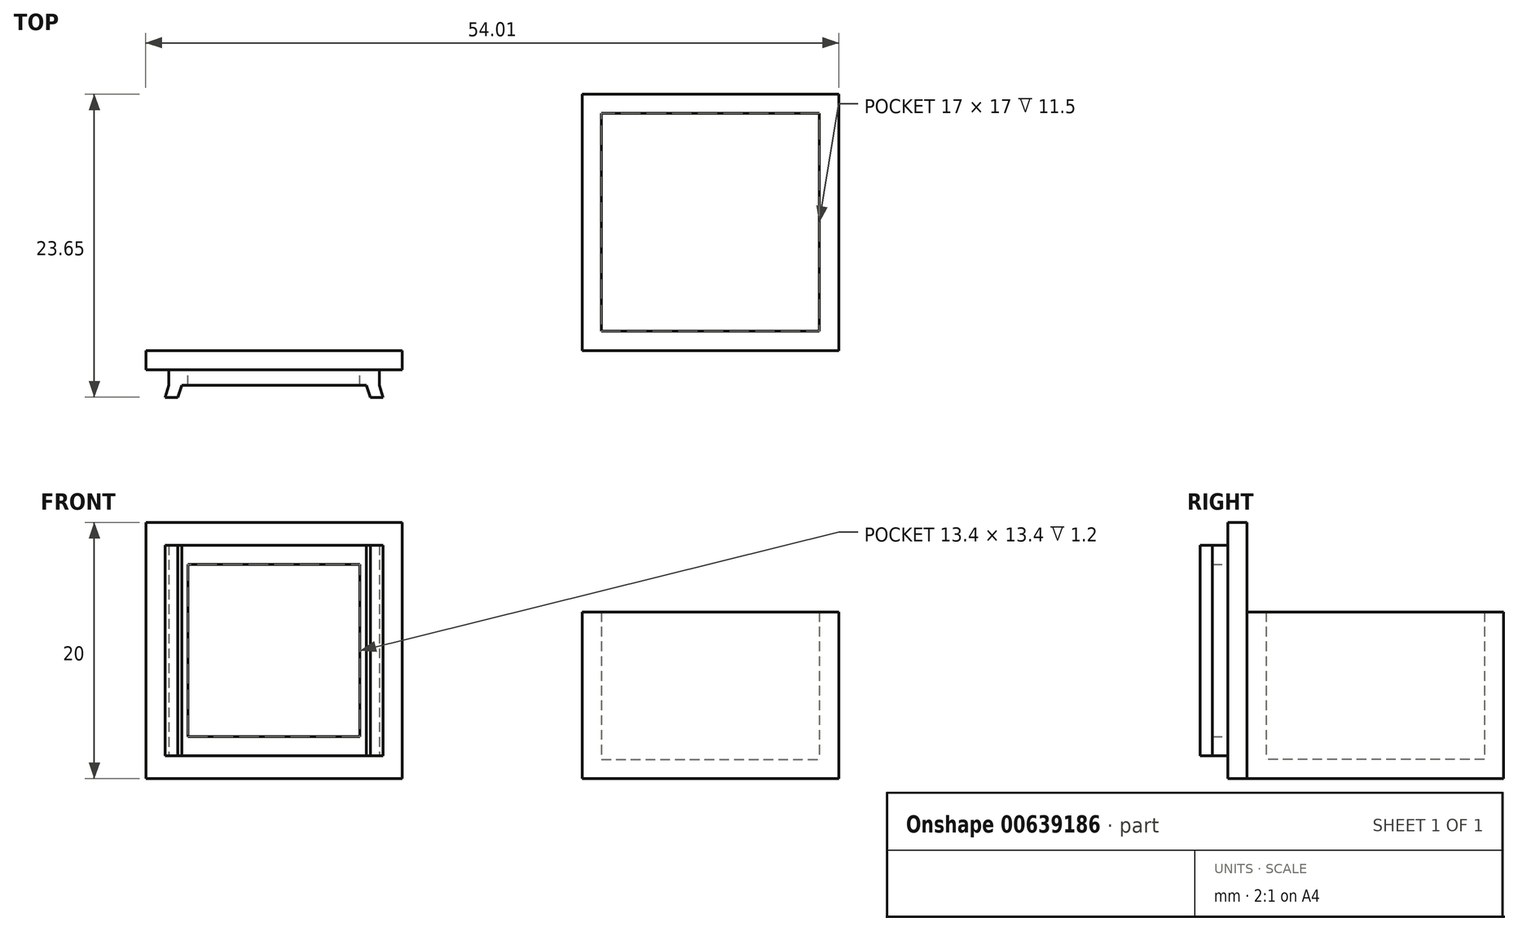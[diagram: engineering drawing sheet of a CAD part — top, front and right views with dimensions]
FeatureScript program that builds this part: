
annotation { "Feature Type Name" : "Feature", "Feature Type Description" : "" }
export const myFeature = defineFeature(function(context is Context, id is Id, definition is map)
    precondition{}
    {
        {
            var Q0;
            Q0=qCreatedBy(makeId("Top.planeOp"),FACE);
            var sketch = newSketch(context, id + "F0", { "sketchPlane" : qUnion([Q0])});
            skLineSegment(sketch, "E0.bottom", {"start": v(0, 0) * mm, "end": v(-20, 0) * mm});
            skLineSegment(sketch, "E0.top", {"start": v(0, 20) * mm, "end": v(-20, 20) * mm});
            skLineSegment(sketch, "E0.left", {"start": v(0, 0) * mm, "end": v(0, 20) * mm});
            skLineSegment(sketch, "E0.right", {"start": v(-20, 0) * mm, "end": v(-20, 20) * mm});
            skSolve(sketch);
        }
        {
            var Q0;
            Q0=makeQuery(id+"F0.imprint","IMPRINT",FACE,{"disambiguationData":[TD([[makeQuery(id+"F0.imprint","IMPRINT",EDGE,{"derivedFrom":sQuery(id+"F0.wireOp",EDGE,"E0.bottom")}),-1.0]])]});
            extrude(context, id + "F1", {"entities" : qUnion([Q0]), "depth" : 1.5 * mm, "offsetDistance" : 25 * mm});
        }
        {
            var Q0;
            Q0=makeQuery(id+"F1.opExtrude","CAP_FACE",FACE,{"disambiguationData":[OSD([sQuery(id+"F0.wireOp",EDGE,"E0.bottom"),sQuery(id+"F0.wireOp",EDGE,"E0.top"),sQuery(id+"F0.wireOp",EDGE,"E0.left"),sQuery(id+"F0.wireOp",EDGE,"E0.right")])],"isStart":false});
            var sketch = newSketch(context, id + "F2", { "sketchPlane" : qUnion([Q0])});
            skLineSegment(sketch, "E1.bottom", {"start": v(-18.5, 18.5) * mm, "end": v(-1.5, 18.5) * mm});
            skLineSegment(sketch, "E1.top", {"start": v(-18.5, 1.5) * mm, "end": v(-1.5, 1.5) * mm});
            skLineSegment(sketch, "E1.left", {"start": v(-18.5, 18.5) * mm, "end": v(-18.5, 1.5) * mm});
            skLineSegment(sketch, "E1.right", {"start": v(-1.5, 18.5) * mm, "end": v(-1.5, 1.5) * mm});
            skSolve(sketch);
        }
        {
            var Q0;
            Q0=makeQuery(id+"F2.imprint","IMPRINT",FACE,{"disambiguationData":[TD([[makeQuery(id+"F2.imprint","IMPRINT",EDGE,{"derivedFrom":sQuery(id+"F2.wireOp",EDGE,"E1.bottom")}),1.0]])]});
            extrude(context, id + "F3", {"entities" : qUnion([Q0]), "operationType" : NewBodyOperationType.ADD, "depth" : 11.5 * mm, "offsetDistance" : 25 * mm});
        }
        {
            var Q0;
            Q0=qCreatedBy(makeId("Front.planeOp"),FACE);
            var sketch = newSketch(context, id + "F4", { "sketchPlane" : qUnion([Q0])});
            skLineSegment(sketch, "E2.bottom", {"start": v(-54, 20) * mm, "end": v(-34, 20) * mm});
            skLineSegment(sketch, "E2.top", {"start": v(-54, 0) * mm, "end": v(-34, 0) * mm});
            skLineSegment(sketch, "E2.left", {"start": v(-54, 20) * mm, "end": v(-54, 0) * mm});
            skLineSegment(sketch, "E2.right", {"start": v(-34, 20) * mm, "end": v(-34, 0) * mm});
            skSolve(sketch);
        }
        {
            var Q0;
            Q0 = qSketchRegion(id + "F4", true);
            var Q1;
            Q1=makeQuery(id+"F4.imprint","IMPRINT",FACE,{"disambiguationData":[TD([[makeQuery(id+"F4.imprint","IMPRINT",EDGE,{"derivedFrom":sQuery(id+"F4.wireOp",EDGE,"E2.bottom")}),-1.0]])]});
            extrude(context, id + "F5", {"entities" : qUnion([Q0, Q1]), "depth" : 1.5 * mm, "offsetDistance" : 25 * mm});
        }
        {
            var Q0;
            Q0=makeQuery(id+"F5.opExtrude","CAP_FACE",FACE,{"disambiguationData":[OSD([sQuery(id+"F4.wireOp",EDGE,"E2.bottom"),sQuery(id+"F4.wireOp",EDGE,"E2.top"),sQuery(id+"F4.wireOp",EDGE,"E2.left"),sQuery(id+"F4.wireOp",EDGE,"E2.right")])],"isStart":false});
            var sketch = newSketch(context, id + "F6", { "sketchPlane" : qUnion([Q0])});
            skLineSegment(sketch, "E3.bottom", {"start": v(-52.2, 18.2) * mm, "end": v(-35.8, 18.2) * mm});
            skLineSegment(sketch, "E3.top", {"start": v(-52.2, 1.8) * mm, "end": v(-35.8, 1.8) * mm});
            skLineSegment(sketch, "E3.left", {"start": v(-52.2, 18.2) * mm, "end": v(-52.2, 1.8) * mm});
            skLineSegment(sketch, "E3.right", {"start": v(-35.8, 18.2) * mm, "end": v(-35.8, 1.8) * mm});
            skLineSegment(sketch, "E4.0", {"start": v(-50.7, 16.7) * mm, "end": v(-37.3, 16.7) * mm});
            skLineSegment(sketch, "E4.1", {"start": v(-50.7, 16.7) * mm, "end": v(-50.7, 3.3) * mm});
            skLineSegment(sketch, "E4.2", {"start": v(-50.7, 3.3) * mm, "end": v(-37.3, 3.3) * mm});
            skLineSegment(sketch, "E4.3", {"start": v(-37.3, 16.7) * mm, "end": v(-37.3, 3.3) * mm});
            skLineSegment(sketch, "E5.0", {"start": v(-59, 25) * mm, "end": v(-59, -5) * mm});
            skLineSegment(sketch, "E5.1", {"start": v(-29, 25) * mm, "end": v(-59, 25) * mm});
            skLineSegment(sketch, "E5.2", {"start": v(-29, -5) * mm, "end": v(-29, 25) * mm});
            skLineSegment(sketch, "E5.3", {"start": v(-59, -5) * mm, "end": v(-29, -5) * mm});
            skSolve(sketch);
        }
        {
            var Q0;
            Q0=makeQuery(id+"F6.imprint","IMPRINT",FACE,{"disambiguationData":[TD([[makeQuery(id+"F6.imprint","IMPRINT",EDGE,{"derivedFrom":sQuery(id+"F6.wireOp",EDGE,"E3.bottom")}),-1.0]])]});
            extrude(context, id + "F7", {"entities" : qUnion([Q0]), "operationType" : NewBodyOperationType.ADD, "depth" : 1.2 * mm, "offsetDistance" : 25 * mm});
        }
        {
            var Q0;
            Q0=makeQuery(id+"F7.opExtrude","SWEPT_FACE",FACE,{"disambiguationData":[OSD([sQuery(id+"F6.wireOp",EDGE,"E3.top")])]});
            var sketch = newSketch(context, id + "F8", { "sketchPlane" : qUnion([Q0])});
            skLineSegment(sketch, "E6", {"start": v(-52.2, 2.7) * mm, "end": v(-52.5, 3.65) * mm});
            skLineSegment(sketch, "E7", {"start": v(-52.5, 3.65) * mm, "end": v(-51.5, 3.65) * mm});
            skLineSegment(sketch, "E8", {"start": v(-51.5, 3.65) * mm, "end": v(-51.2, 2.7) * mm});
            skLineSegment(sketch, "E9", {"start": v(-51.2, 2.7) * mm, "end": v(-52.2, 2.7) * mm});
            skLineSegment(sketch, "E10", {"start": v(-44, 2.7) * mm, "end": v(-44, 4.56) * mm, "construction": true});
            skLineSegment(sketch, "E11.MirrorCS", {"start": v(-36.51, 3.65) * mm, "end": v(-36.8, 2.7) * mm});
            skLineSegment(sketch, "E12.MirrorCS", {"start": v(-35.51, 3.65) * mm, "end": v(-36.51, 3.65) * mm});
            skLineSegment(sketch, "E13.MirrorCS", {"start": v(-35.8, 2.7) * mm, "end": v(-35.51, 3.65) * mm});
            skLineSegment(sketch, "E14.MirrorCS", {"start": v(-36.8, 2.7) * mm, "end": v(-35.8, 2.7) * mm});
            skSolve(sketch);
        }
        {
            var Q0;
            Q0 = qSketchRegion(id + "F8", true);
            extrude(context, id + "F9", {"entities" : qUnion([Q0]), "operationType" : NewBodyOperationType.ADD, "oppositeDirection" : true, "depth" : 16.4 * mm, "offsetDistance" : 25 * mm});
        }
    });
